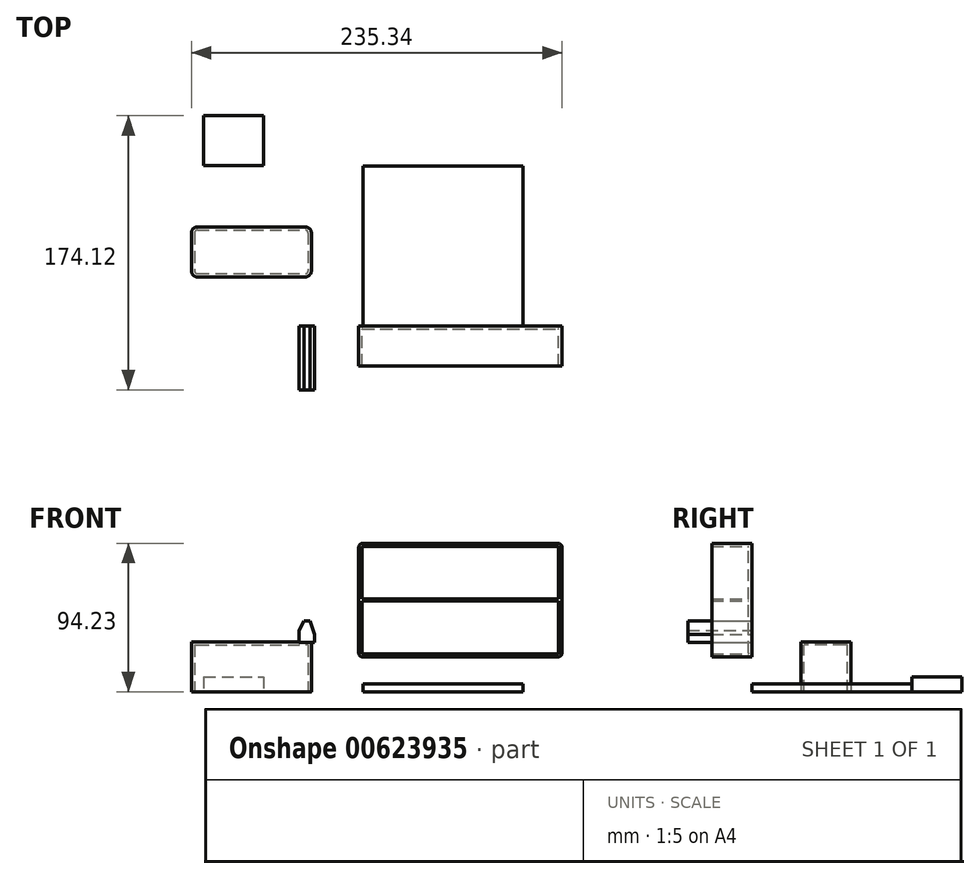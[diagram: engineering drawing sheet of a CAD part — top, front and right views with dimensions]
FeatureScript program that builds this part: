
annotation { "Feature Type Name" : "Feature", "Feature Type Description" : "" }
export const myFeature = defineFeature(function(context is Context, id is Id, definition is map)
    precondition{}
    {
        {
            var Q0;
            Q0=qCreatedBy(makeId("Top.planeOp"),FACE);
            var sketch = newSketch(context, id + "F0", { "sketchPlane" : qUnion([Q0])});
            skLineSegment(sketch, "E0.bottom", {"start": v(0, 0) * mm, "end": v(101.6, 0) * mm});
            skLineSegment(sketch, "E0.top", {"start": v(0, 101.6) * mm, "end": v(101.6, 101.6) * mm});
            skLineSegment(sketch, "E0.left", {"start": v(0, 0) * mm, "end": v(0, 101.6) * mm});
            skLineSegment(sketch, "E0.right", {"start": v(101.6, 0) * mm, "end": v(101.6, 101.6) * mm});
            skSolve(sketch);
        }
        {
            var Q0;
            Q0=qSketchRegion(id+"F0",true);
            extrude(context, id + "F1", {"entities" : qUnion([Q0]), "depth" : 5.08 * mm});
        }
        {
            var Q0;
            Q0=qCreatedBy(makeId("Front.planeOp"),FACE);
            var sketch = newSketch(context, id + "F2", { "sketchPlane" : qUnion([Q0])});
            skLineSegment(sketch, "E1", {"start": v(-40.41, 31.28) * mm, "end": v(-40.41, 38.9) * mm});
            skLineSegment(sketch, "E2", {"start": v(-40.41, 38.9) * mm, "end": v(-37.24, 45.08) * mm});
            skLineSegment(sketch, "E3", {"start": v(-37.24, 45.08) * mm, "end": v(-33.43, 45.08) * mm});
            skLineSegment(sketch, "E4", {"start": v(-33.43, 45.08) * mm, "end": v(-30.61, 36.36) * mm});
            skLineSegment(sketch, "E5", {"start": v(-30.61, 36.36) * mm, "end": v(-30.61, 31.28) * mm});
            skLineSegment(sketch, "E6", {"start": v(-30.61, 31.28) * mm, "end": v(-40.41, 31.28) * mm});
            skSolve(sketch);
        }
        {
            var Q0;
            Q0=qSketchRegion(id+"F2",true);
            extrude(context, id + "F3", {"entities" : qUnion([Q0]), "depth" : 40.64 * mm});
        }
        {
            var Q0;
            Q0=qCreatedBy(makeId("Front.planeOp"),FACE);
            var sketch = newSketch(context, id + "F4", { "sketchPlane" : qUnion([Q0])});
            skLineSegment(sketch, "E7.bottom", {"start": v(-2.57, 22.1) * mm, "end": v(126.46, 22.1) * mm});
            skLineSegment(sketch, "E7.top", {"start": v(-2.57, 94.23) * mm, "end": v(126.46, 94.23) * mm});
            skLineSegment(sketch, "E7.left", {"start": v(-2.57, 22.1) * mm, "end": v(-2.57, 94.23) * mm});
            skLineSegment(sketch, "E7.right", {"start": v(126.46, 22.1) * mm, "end": v(126.46, 94.23) * mm});
            skSolve(sketch);
        }
        {
            var Q0;
            Q0=qSketchRegion(id+"F4",true);
            extrude(context, id + "F5", {"entities" : qUnion([Q0]), "depth" : 25.4 * mm});
        }
        {
            var Q0;
            Q0=makeQuery(id+"F5.opExtrude","SWEPT_EDGE",EDGE,{"disambiguationData":[OSD([sQuery(id+"F4.wireOp",EDGE,"E7.bottom"),sQuery(id+"F4.wireOp",EDGE,"E7.left")])]});
            var Q1;
            Q1=makeQuery(id+"F5.opExtrude","SWEPT_EDGE",EDGE,{"disambiguationData":[OSD([sQuery(id+"F4.wireOp",EDGE,"E7.top"),sQuery(id+"F4.wireOp",EDGE,"E7.left")])]});
            var Q2;
            Q2=makeQuery(id+"F5.opExtrude","SWEPT_EDGE",EDGE,{"disambiguationData":[OSD([sQuery(id+"F4.wireOp",EDGE,"E7.bottom"),sQuery(id+"F4.wireOp",EDGE,"E7.right")])]});
            var Q3;
            Q3=makeQuery(id+"F5.opExtrude","SWEPT_EDGE",EDGE,{"disambiguationData":[OSD([sQuery(id+"F4.wireOp",EDGE,"E7.top"),sQuery(id+"F4.wireOp",EDGE,"E7.right")])]});
            fillet(context, id + "F6", {"entities" : qUnion([Q0, Q1, Q2, Q3]), "radius" : 2.54 * mm, "tangentPropagation" : true, "allowEdgeOverflow" : false});
        }
        {
            var Q0;
            Q0=makeQuery(id+"F5.opExtrude","CAP_FACE",FACE,{"disambiguationData":[OSD([sQuery(id+"F4.wireOp",EDGE,"E7.bottom"),sQuery(id+"F4.wireOp",EDGE,"E7.top"),sQuery(id+"F4.wireOp",EDGE,"E7.left"),sQuery(id+"F4.wireOp",EDGE,"E7.right")])],"isStart":false});
            shell(context, id + "F7", {"entities" : qUnion([Q0]), "thickness" : 2.03 * mm});
        }
        {
            var Q0;
            Q0=makeQuery(id+"F7.opShell","OFFSET_FACE",FACE,{"disambiguationData":[OSD([sQuery(id+"F4.wireOp",EDGE,"E7.bottom"),sQuery(id+"F4.wireOp",EDGE,"E7.top"),sQuery(id+"F4.wireOp",EDGE,"E7.left"),sQuery(id+"F4.wireOp",EDGE,"E7.right")])]});
            var sketch = newSketch(context, id + "F8", { "sketchPlane" : qUnion([Q0])});
            skLineSegment(sketch, "E8", {"start": v(-0.54, 58.16) * mm, "end": v(124.43, 58.16) * mm, "construction": true});
            skLineSegment(sketch, "E9", {"start": v(-0.54, 57.53) * mm, "end": v(124.43, 57.53) * mm});
            skLineSegment(sketch, "E10.MirrorCS", {"start": v(-0.54, 58.8) * mm, "end": v(124.43, 58.8) * mm});
            skLineSegment(sketch, "E11", {"start": v(-0.54, 57.53) * mm, "end": v(-0.54, 58.8) * mm});
            skLineSegment(sketch, "E12", {"start": v(124.43, 57.53) * mm, "end": v(124.43, 58.8) * mm});
            skSolve(sketch);
        }
        {
            var Q0;
            Q0=qSketchRegion(id+"F8",true);
            var Q1;
            Q1=makeQuery(id+"F5.opExtrude","CAP_FACE",FACE,{"disambiguationData":[OSD([sQuery(id+"F4.wireOp",EDGE,"E7.bottom"),sQuery(id+"F4.wireOp",EDGE,"E7.top"),sQuery(id+"F4.wireOp",EDGE,"E7.left"),sQuery(id+"F4.wireOp",EDGE,"E7.right")])],"isStart":false});
            extrude(context, id + "F9", {"entities" : qUnion([Q0]), "operationType" : NewBodyOperationType.ADD, "endBound" : BoundingType.UP_TO_SURFACE, "endBoundEntityFace" : qUnion([Q1]), "depth" : 25.4 * mm});
        }
        {
            var Q0;
            Q0=qCreatedBy(makeId("Top.planeOp"),FACE);
            var sketch = newSketch(context, id + "F10", { "sketchPlane" : qUnion([Q0])});
            skLineSegment(sketch, "E13.bottom", {"start": v(-108.88, 62.86) * mm, "end": v(-32.68, 62.86) * mm});
            skLineSegment(sketch, "E13.top", {"start": v(-108.88, 31.1) * mm, "end": v(-32.68, 31.1) * mm});
            skLineSegment(sketch, "E13.left", {"start": v(-108.88, 62.86) * mm, "end": v(-108.88, 31.1) * mm});
            skLineSegment(sketch, "E13.right", {"start": v(-32.68, 62.86) * mm, "end": v(-32.68, 31.1) * mm});
            skSolve(sketch);
        }
        {
            var Q0;
            Q0=qSketchRegion(id+"F10",true);
            extrude(context, id + "F11", {"entities" : qUnion([Q0]), "depth" : 31.75 * mm});
        }
        {
            var Q0;
            Q0=makeQuery(id+"F11.opExtrude","SWEPT_EDGE",EDGE,{"disambiguationData":[OSD([sQuery(id+"F10.wireOp",EDGE,"E13.top"),sQuery(id+"F10.wireOp",EDGE,"E13.left")])]});
            var Q1;
            Q1=makeQuery(id+"F11.opExtrude","SWEPT_EDGE",EDGE,{"disambiguationData":[OSD([sQuery(id+"F10.wireOp",EDGE,"E13.bottom"),sQuery(id+"F10.wireOp",EDGE,"E13.left")])]});
            var Q2;
            Q2=makeQuery(id+"F11.opExtrude","SWEPT_EDGE",EDGE,{"disambiguationData":[OSD([sQuery(id+"F10.wireOp",EDGE,"E13.bottom"),sQuery(id+"F10.wireOp",EDGE,"E13.right")])]});
            var Q3;
            Q3=makeQuery(id+"F11.opExtrude","SWEPT_EDGE",EDGE,{"disambiguationData":[OSD([sQuery(id+"F10.wireOp",EDGE,"E13.top"),sQuery(id+"F10.wireOp",EDGE,"E13.right")])]});
            fillet(context, id + "F12", {"entities" : qUnion([Q0, Q1, Q2, Q3]), "radius" : 3.8 * mm, "tangentPropagation" : true, "allowEdgeOverflow" : false});
        }
        {
            var Q0;
            Q0=makeQuery(id+"F11.opExtrude","CAP_FACE",FACE,{"disambiguationData":[OSD([sQuery(id+"F10.wireOp",EDGE,"E13.bottom"),sQuery(id+"F10.wireOp",EDGE,"E13.top"),sQuery(id+"F10.wireOp",EDGE,"E13.left"),sQuery(id+"F10.wireOp",EDGE,"E13.right")])],"isStart":true});
            shell(context, id + "F13", {"entities" : qUnion([Q0]), "thickness" : 2.03 * mm});
        }
        {
            var Q0;
            Q0=qCreatedBy(makeId("Top.planeOp"),FACE);
            var sketch = newSketch(context, id + "F14", { "sketchPlane" : qUnion([Q0])});
            skLineSegment(sketch, "E14.bottom", {"start": v(-101, 101.73) * mm, "end": v(-62.9, 101.73) * mm});
            skLineSegment(sketch, "E14.top", {"start": v(-101, 133.48) * mm, "end": v(-62.9, 133.48) * mm});
            skLineSegment(sketch, "E14.left", {"start": v(-101, 101.73) * mm, "end": v(-101, 133.48) * mm});
            skLineSegment(sketch, "E14.right", {"start": v(-62.9, 101.73) * mm, "end": v(-62.9, 133.48) * mm});
            skSolve(sketch);
        }
        {
            var Q0;
            Q0=qSketchRegion(id+"F14",true);
            extrude(context, id + "F15", {"entities" : qUnion([Q0]), "depth" : 9.52 * mm});
        }
    });
